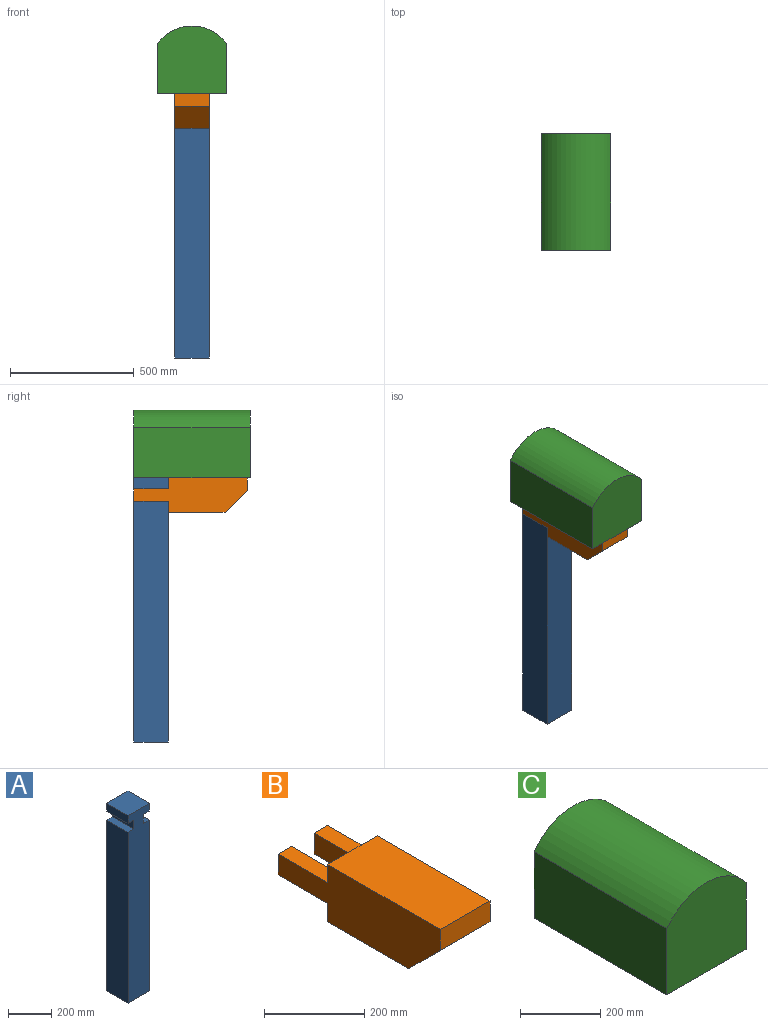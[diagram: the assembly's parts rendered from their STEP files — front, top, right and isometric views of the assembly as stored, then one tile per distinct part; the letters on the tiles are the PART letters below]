
ASSEMBLY  parts=3 mates=2
PART A: 14 faces, bbox 139.7x139.7x1066.8 mm
  f0: plane 139.7x44.45mm, normal (-1,0,0), area 6209.7mm2, adj f1,f3,f7,f11
  f1: plane 1066.8x139.7mm, normal (0,-1,0), area 145161mm2, adj f0,f2,f3,f4,f5,f6,f8,f9
  f2: plane 971.55x139.7mm, normal (1,0,0), area 135725.5mm2, adj f1,f5,f7,f9
  f3: plane 139.7x139.7mm, normal (0,0,1), area 19516.1mm2, adj f0,f1,f6,f7
  f4: plane 971.55x139.7mm, normal (-1,0,0), area 135725.5mm2, adj f1,f5,f7,f12
  f5: plane 139.7x139.7mm, normal (0,0,-1), area 19516.1mm2, adj f1,f2,f4,f7
  f6: plane 139.7x44.45mm, normal (1,0,0), area 6209.7mm2, adj f1,f3,f7,f8
  f7: plane 1066.8x139.7mm, normal (0,1,0), area 145161mm2, adj f0,f2,f3,f4,f5,f6,f8,f9
  f8: plane 139.7x38.1mm, normal (0,0,-1), area 5322.6mm2, adj f1,f6,f7,f10
  f9: plane 139.7x38.1mm, normal (0,0,1), area 5322.6mm2, adj f1,f2,f7,f10
  f10: plane 139.7x50.8mm, normal (1,0,0), area 7096.8mm2, adj f1,f7,f8,f9
  f11: plane 139.7x38.1mm, normal (0,0,-1), area 5322.6mm2, adj f0,f1,f7,f13
  f12: plane 139.7x38.1mm, normal (0,0,1), area 5322.6mm2, adj f1,f4,f7,f13
  f13: plane 139.7x50.8mm, normal (-1,0,0), area 7096.8mm2, adj f1,f7,f11,f12
PART B: 15 faces, bbox 139.7x457.2x139.7 mm
  f0: plane 457.2x139.7mm, normal (-1,0,0), area 47499.9mm2, adj f1,f3,f5,f6,f10,f12,f13,f14
  f1: plane 139.7x50.8mm, normal (0,-1,0), area 7096.8mm2, adj f0,f2,f6,f14
  f2: plane 457.2x139.7mm, normal (1,0,0), area 47499.9mm2, adj f1,f3,f4,f6,f7,f9,f13,f14
  f3: plane 228.6x139.7mm, normal (0,0,-1), area 31935.4mm2, adj f0,f2,f13,f14
  f4: plane 50.8x38.1mm, normal (0,1,0), area 1935.5mm2, adj f2,f7,f8,f9
  f5: plane 50.8x38.1mm, normal (0,1,0), area 1935.5mm2, adj f0,f10,f11,f12
  f6: plane 317.5x139.7mm, normal (0,0,1), area 44354.7mm2, adj f0,f1,f2,f13
  f7: plane 139.7x38.1mm, normal (0,0,1), area 5322.6mm2, adj f2,f4,f8,f13
  f8: plane 139.7x50.8mm, normal (-1,0,0), area 7096.8mm2, adj f4,f7,f9,f13
  f9: plane 139.7x38.1mm, normal (0,0,-1), area 5322.6mm2, adj f2,f4,f8,f13
  f10: plane 139.7x38.1mm, normal (0,0,-1), area 5322.6mm2, adj f0,f5,f11,f13
  f11: plane 139.7x50.8mm, normal (1,0,0), area 7096.8mm2, adj f5,f10,f12,f13
  f12: plane 139.7x38.1mm, normal (0,0,1), area 5322.6mm2, adj f0,f5,f11,f13
  f13: plane 139.7x139.7mm, normal (0,1,0), area 15645.1mm2, adj f0,f2,f3,f6,f7,f8,f9,f10
  f14: plane 139.7x88.9mm, normal (0,-0.71,-0.71), area 17563.6mm2, adj f0,f1,f2,f3
PART C: 6 faces, bbox 279.4x469.9x274.3 mm
  f0: plane 469.9x203.2mm, normal (-1,0,0), area 95483.7mm2, adj f1,f3,f4,f5
  f1: plane 469.9x279.4mm, normal (0,0,-1), area 131290.1mm2, adj f0,f2,f4,f5
  f2: plane 469.9x203.2mm, normal (1,0,0), area 95483.7mm2, adj f1,f3,f4,f5
  f3: cylinder r=172.74mm len=469.9mm, axis (0,-1,0), area 152924.1mm2, adj f0,f2,f4,f5
  f4: plane 279.4x274.34mm, normal (0,1,0), area 70688.6mm2, adj f0,f1,f2,f3
  f5: plane 279.4x274.34mm, normal (0,-1,0), area 70688.6mm2, adj f0,f1,f2,f3
PLACE A t=(-260.79,83.64,928.99)mm fixed
PLACE B t=(-260.79,223.34,928.99)mm
PLACE C t=(-330.64,-246.56,928.99)mm
MATE fastened C.f4 <-> A.f7  axis (0,1,0) through (-190.94,223.34,928.99)mm
MATE fastened B.f2 <-> A.f6  axis (1,0,0) through (-121.09,83.64,928.99)mm
